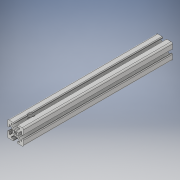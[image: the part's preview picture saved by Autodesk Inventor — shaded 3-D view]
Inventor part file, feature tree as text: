
AUTODESK INVENTOR PART (.ipt)
format: ipt  version: 2018 (Build 220112000, 112)  size: 324,096 bytes
history: native  units: in
note: dims shown in document units (in); Inventor stores cm internally (conversion verified against a paired STEP export)
features: direct_edit x1, extrude x1, sketch x1, projected_geometry x1, other x1, move_body x1
ambient origin geometry x8: Origin, YZ Plane, XZ Plane, XY Plane, X Axis, Y Axis, Z Axis, Center Point
bodies: Solid1 (feature_tree)
feature tree (6):
  direct_edit  "Direct Edit1"
  extrude  "Extrusion1"  Depth=1.5in
  sketch  "Sketch1"  dims[d0=0.0in d1=0.0in d2=14.0in d3=1.5in d4=0.5312in d5=1.0in d6=0.0in]
  projected_geometry  "Projected Loop1"
  other  "8020-1515-S-1515-S X 145_1_1:1"
  move_body  "Move1"
